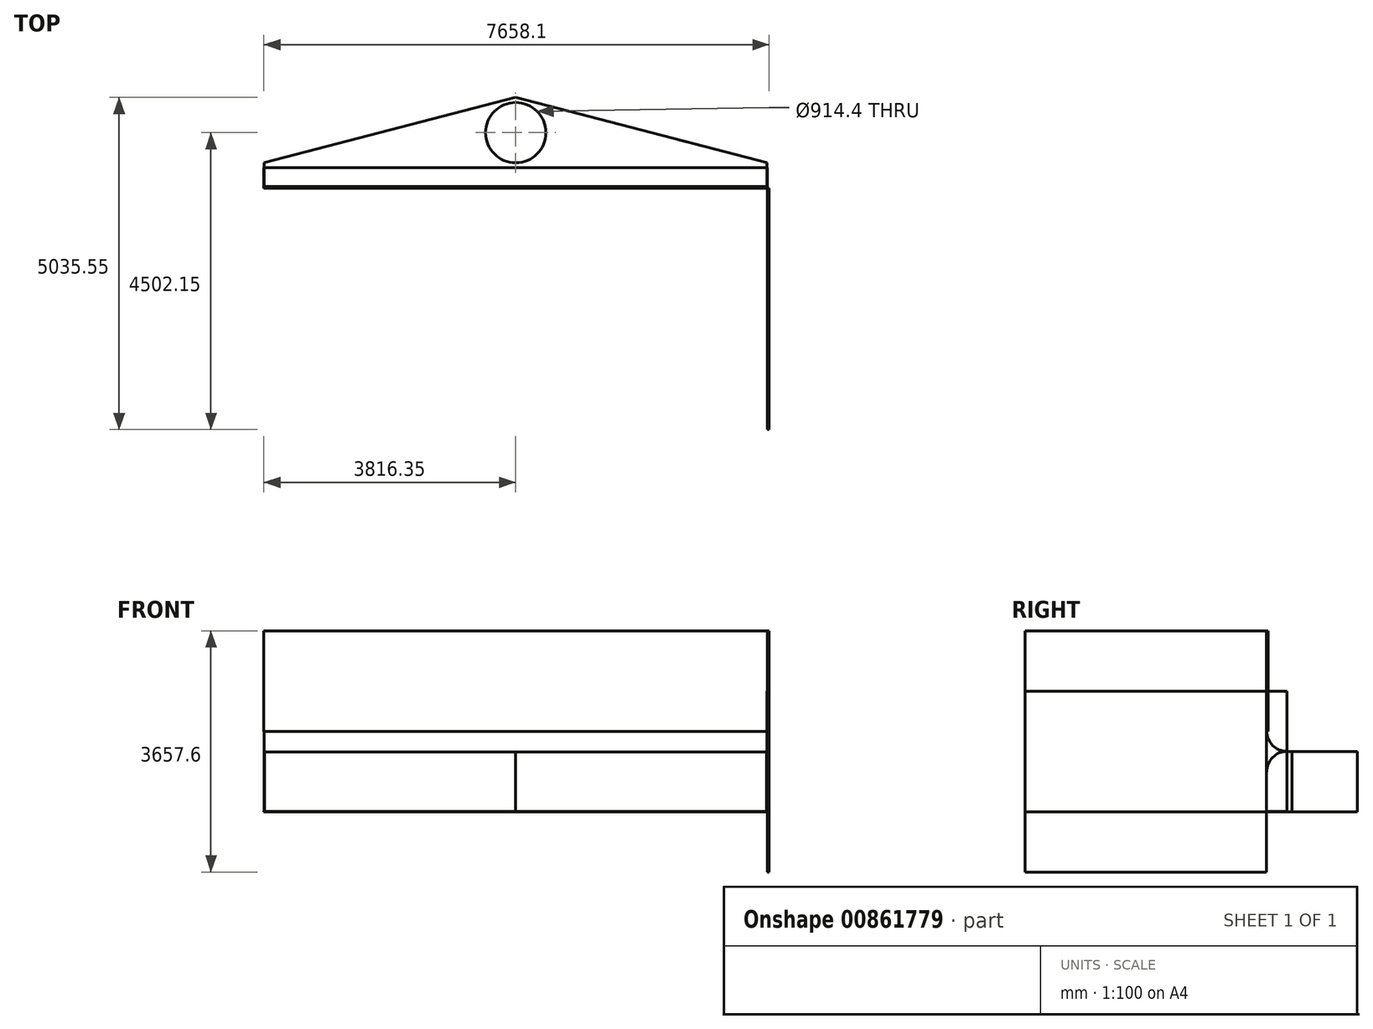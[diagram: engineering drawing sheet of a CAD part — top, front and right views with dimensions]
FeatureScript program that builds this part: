
annotation { "Feature Type Name" : "Feature", "Feature Type Description" : "" }
export const myFeature = defineFeature(function(context is Context, id is Id, definition is map)
    precondition{}
    {
        {
            var Q0;
            Q0=qCreatedBy(makeId("Front.planeOp"),FACE);
            var sketch = newSketch(context, id + "F0", { "sketchPlane" : qUnion([Q0])});
            skLineSegment(sketch, "E0", {"start": v(0, 0) * mm, "end": v(7620, 0) * mm});
            skLineSegment(sketch, "E1", {"start": v(7620, 0) * mm, "end": v(7620, 914.4) * mm});
            skLineSegment(sketch, "E2", {"start": v(7620, 914.4) * mm, "end": v(0, 914.4) * mm});
            skLineSegment(sketch, "E3", {"start": v(0, 914.4) * mm, "end": v(0, 0) * mm});
            skSolve(sketch);
        }
        {
            var Q0;
            Q0=makeQuery(id+"F0.imprint","IMPRINT",FACE,{"disambiguationData":[TD([[makeQuery(id+"F0.imprint","IMPRINT",EDGE,{"derivedFrom":sQuery(id+"F0.wireOp",EDGE,"E0")}),1.0]])]});
            extrude(context, id + "F1", {"entities" : qUnion([Q0]), "depth" : 1066.8 * mm, "offsetDistance" : 25.4 * mm});
        }
        {
            var Q0;
            Q0=makeQuery(id+"F1.opExtrude","SWEPT_FACE",FACE,{"disambiguationData":[OSD([sQuery(id+"F0.wireOp",EDGE,"E2")])]});
            var sketch = newSketch(context, id + "F2", { "sketchPlane" : qUnion([Q0])});
            skLineSegment(sketch, "E4", {"start": v(3810, 0) * mm, "end": v(3810, -533.4) * mm, "construction": true});
            skCircle(sketch, "E5", {"center": v(3810, -533.4) * mm, "radius": 457.2 * mm});
            skLineSegment(sketch, "E6.0", {"start": v(7620, -990.6) * mm, "end": v(0, -990.6) * mm, "construction": true});
            skLineSegment(sketch, "E7", {"start": v(3810, 0) * mm, "end": v(7620, -990.6) * mm});
            skLineSegment(sketch, "E8", {"start": v(3810, 0) * mm, "end": v(0, -990.6) * mm});
            skSolve(sketch);
        }
        {
            var Q0;
            {var subQ0=sQuery(id+"F2.wireOp",EDGE,"E7");Q0=makeQuery(id+"F2.imprint","IMPRINT",FACE,{"disambiguationData":[TD([[makeQuery(id+"F2.imprint","IMPRINT",EDGE,{"derivedFrom":subQ0}),1.0]])]});}
            var Q1;
            {var subQ0=sQuery(id+"F2.wireOp",EDGE,"E8");Q1=makeQuery(id+"F2.imprint","IMPRINT",FACE,{"disambiguationData":[TD([[makeQuery(id+"F2.imprint","IMPRINT",EDGE,{"derivedFrom":subQ0}),-1.0]])]});}
            var Q2;
            Q2=sQuery(id+"F2.wireOp",EDGE,"E7");
            extrude(context, id + "F3", {"entities" : qUnion([Q0, Q1]), "operationType" : NewBodyOperationType.REMOVE, "surfaceEntities" : qUnion([Q2]), "endBound" : BoundingType.THROUGH_ALL, "oppositeDirection" : true, "depth" : 25.4 * mm, "offsetDistance" : 25.4 * mm});
        }
        {
            var Q0;
            Q0=makeQuery(id+"F1.opExtrude","CAP_FACE",FACE,{"disambiguationData":[OSD([sQuery(id+"F0.wireOp",EDGE,"E0"),sQuery(id+"F0.wireOp",EDGE,"E1"),sQuery(id+"F0.wireOp",EDGE,"E2"),sQuery(id+"F0.wireOp",EDGE,"E3")])],"isStart":false});
            shell(context, id + "F4", {"entities" : qUnion([Q0]), "thickness" : 6.35 * mm});
        }
        {
            var Q0;
            Q0=makeQuery(id+"F2.imprint","IMPRINT",FACE,{"disambiguationData":[TD([[makeQuery(id+"F2.imprint","IMPRINT",EDGE,{"derivedFrom":sQuery(id+"F2.wireOp",EDGE,"E5")}),1.0]])]});
            extrude(context, id + "F5", {"entities" : qUnion([Q0]), "operationType" : NewBodyOperationType.REMOVE, "endBound" : BoundingType.UP_TO_NEXT, "oppositeDirection" : true, "depth" : 25.4 * mm, "offsetDistance" : 25.4 * mm});
        }
        {
            var Q0;
            Q0=makeQuery(id+"F1.opExtrude","SWEPT_FACE",FACE,{"disambiguationData":[OSD([sQuery(id+"F0.wireOp",EDGE,"E1")])]});
            var sketch = newSketch(context, id + "F6", { "sketchPlane" : qUnion([Q0])});
            skLineSegment(sketch, "E9", {"start": v(-1066.8, 914.4) * mm, "end": v(-1066.8, 1219.2) * mm, "construction": true});
            skArc(sketch, "E10", {"start": v(-1371.6, 1219.2) * mm, "mid": v(-1282.33, 1003.67) * mm, "end": v(-1066.8, 914.4) * mm});
            skLineSegment(sketch, "E11", {"start": v(-1066.8, 1219.2) * mm, "end": v(-1371.6, 1219.2) * mm, "construction": true});
            skArc(sketch, "E12.0", {"start": v(-1377.95, 1219.2) * mm, "mid": v(-1286.82, 999.18) * mm, "end": v(-1066.8, 908.05) * mm});
            skLineSegment(sketch, "E13", {"start": v(-1066.8, 908.05) * mm, "end": v(-1066.8, 914.4) * mm});
            skLineSegment(sketch, "E14", {"start": v(-1371.6, 1219.2) * mm, "end": v(-1377.95, 1219.2) * mm});
            skSolve(sketch);
        }
        {
            var Q0;
            Q0 = qSketchRegion(id + "F6", true);
            var Q1;
            Q1=makeQuery(id+"F1.opExtrude","CAP_VERTEX",VERTEX,{"disambiguationData":[OSD([sQuery(id+"F0.wireOp",EDGE,"E2"),sQuery(id+"F0.wireOp",EDGE,"E3")])],"isStart":false});
            extrude(context, id + "F7", {"entities" : qUnion([Q0]), "endBound" : BoundingType.UP_TO_VERTEX, "oppositeDirection" : true, "depth" : 25.4 * mm, "endBoundEntityVertex" : qUnion([Q1]), "offsetDistance" : 25.4 * mm});
        }
        {
            var Q0;
            Q0=makeQuery(id+"F7.opExtrude","CAP_FACE",FACE,{"disambiguationData":[OSD([sQuery(id+"F6.wireOp",EDGE,"E10"),sQuery(id+"F6.wireOp",EDGE,"E12.0"),sQuery(id+"F6.wireOp",EDGE,"E13"),sQuery(id+"F6.wireOp",EDGE,"E14")])],"isStart":true});
            var sketch = newSketch(context, id + "F8", { "sketchPlane" : qUnion([Q0])});
            skLineSegment(sketch, "E15", {"start": v(-1377.95, 1219.2) * mm, "end": v(-1377.95, 0) * mm});
            skLineSegment(sketch, "E16.1", {"start": v(-1066.8, 0) * mm, "end": v(-1066.8, 914.4) * mm});
            skLineSegment(sketch, "E17.1", {"start": v(-1371.6, 1219.2) * mm, "end": v(-1377.95, 1219.2) * mm});
            skArc(sketch, "E17.2", {"start": v(-1371.6, 1219.2) * mm, "mid": v(-1282.33, 1003.67) * mm, "end": v(-1066.8, 914.4) * mm});
            skLineSegment(sketch, "E18", {"start": v(-1066.8, 0) * mm, "end": v(-1377.95, 0) * mm});
            skSolve(sketch);
        }
        {
            var Q0;
            Q0=makeQuery(id+"F8.imprint","IMPRINT",FACE,{"disambiguationData":[TD([[makeQuery(id+"F8.imprint","IMPRINT",EDGE,{"derivedFrom":sQuery(id+"F8.wireOp",EDGE,"E17.1")}),1.0]])]});
            var Q1;
            Q1=makeQuery(id+"F8.imprint","IMPRINT",FACE,{"disambiguationData":[TD([[makeQuery(id+"F8.imprint","IMPRINT",EDGE,{"derivedFrom":sQuery(id+"F8.wireOp",EDGE,"E15")}),1.0]])]});
            extrude(context, id + "F9", {"entities" : qUnion([Q0, Q1]), "depth" : 6.35 * mm, "offsetDistance" : 25.4 * mm});
        }
        {
            var Q0;
            {var subQ0=sQuery(id+"F2.wireOp",EDGE,"E8");var subQ1=sQuery(id+"F2.wireOp",EDGE,"E7");var subQ2=sQuery(id+"F0.wireOp",EDGE,"E2");Q0=makeQuery(id+"F3.boolean.opBoolean","TWEAK_EDGE",EDGE,{"derivedFrom":[makeQuery(id+"F3.opExtrude","SWEPT_EDGE",EDGE,{"disambiguationData":[OSD([subQ2,subQ1,subQ0]),OD(0.0)]}),makeQuery(id+"F3.opExtrude","SWEPT_EDGE",EDGE,{"disambiguationData":[OSD([subQ2,subQ1,subQ0]),OD(1.0)]})]});}
            var Q1;
            Q1=sQuery(id+"F2.wireOp",EDGE,"E4");
            cPlane(context, id + "F10", {"entities" : qUnion([Q0, Q1]), "cplaneType" : CPlaneType.LINE_ANGLE, "offset" : 25.4 * mm, "angle" : 0 * degree, "width" : 152.4 * mm, "height" : 152.4 * mm});
        }
        {
            var Q0;
            Q0=makeQuery(id+"F9.opExtrude","SWEPT_BODY",BODY,{"disambiguationData":[OSD([sQuery(id+"F8.wireOp",EDGE,"E15"),sQuery(id+"F8.wireOp",EDGE,"E16.1"),sQuery(id+"F8.wireOp",EDGE,"E17.1"),sQuery(id+"F8.wireOp",EDGE,"E17.2"),sQuery(id+"F8.wireOp",EDGE,"E17.4"),sQuery(id+"F8.wireOp",EDGE,"E17.5")])]});
            var Q1;
            Q1=qCreatedBy(id+"F10.planeOp",FACE);
            mirror(context, id + "F11", {"entities" : qUnion([Q0]), "mirrorPlane" : qUnion([Q1])});
        }
        {
            var Q0;
            Q0=makeQuery(id+"F9.opExtrude","CAP_FACE",FACE,{"disambiguationData":[OSD([sQuery(id+"F8.wireOp",EDGE,"E15"),sQuery(id+"F8.wireOp",EDGE,"E16.1"),sQuery(id+"F8.wireOp",EDGE,"E17.1"),sQuery(id+"F8.wireOp",EDGE,"E17.2"),sQuery(id+"F8.wireOp",EDGE,"E18")])],"isStart":false});
            var sketch = newSketch(context, id + "F12", { "sketchPlane" : qUnion([Q0])});
            skSolve(sketch);
        }
        {
            var Q0;
            Q0=makeQuery(id+"F1.opExtrude","SWEPT_FACE",FACE,{"disambiguationData":[OSD([sQuery(id+"F0.wireOp",EDGE,"E0")])]});
            var sketch = newSketch(context, id + "F13", { "sketchPlane" : qUnion([Q0])});
            skLineSegment(sketch, "E19.bottom", {"start": v(-6.35, 1066.8) * mm, "end": v(7626.35, 1066.8) * mm});
            skLineSegment(sketch, "E19.top", {"start": v(-6.35, 1377.95) * mm, "end": v(7626.35, 1377.95) * mm});
            skLineSegment(sketch, "E19.left", {"start": v(-6.35, 1066.8) * mm, "end": v(-6.35, 1377.95) * mm});
            skLineSegment(sketch, "E19.right", {"start": v(7626.35, 1066.8) * mm, "end": v(7626.35, 1377.95) * mm});
            skSolve(sketch);
        }
        {
            var Q0;
            Q0=makeQuery(id+"F13.imprint","IMPRINT",FACE,{"disambiguationData":[TD([[makeQuery(id+"F13.imprint","IMPRINT",EDGE,{"derivedFrom":sQuery(id+"F13.wireOp",EDGE,"E19.top")}),-1.0]])]});
            extrude(context, id + "F14", {"entities" : qUnion([Q0]), "oppositeDirection" : true, "depth" : 6.35 * mm, "offsetDistance" : 25.4 * mm});
        }
        {
            var Q0;
            Q0=makeQuery(id+"F12.imprint","IMPRINT",FACE,{"disambiguationData":[TD([[makeQuery(id+"F12.imprint","IMPRINT",EDGE,{"derivedFrom":makeQuery(id+"F9.opExtrude","CAP_EDGE",EDGE,{"disambiguationData":[OSD([sQuery(id+"F8.wireOp",EDGE,"E15")])],"isStart":false})}),1.0]])]});
            var sketch = newSketch(context, id + "F15", { "sketchPlane" : qUnion([Q0])});
            skLineSegment(sketch, "E20.bottom", {"start": v(-1377.95, 2743.2) * mm, "end": v(-5035.55, 2743.2) * mm});
            skLineSegment(sketch, "E20.top", {"start": v(-1377.95, 0) * mm, "end": v(-5035.55, 0) * mm});
            skLineSegment(sketch, "E20.left", {"start": v(-1377.95, 2743.2) * mm, "end": v(-1377.95, 0) * mm});
            skLineSegment(sketch, "E20.right", {"start": v(-5035.55, 2743.2) * mm, "end": v(-5035.55, 0) * mm});
            skSolve(sketch);
        }
        {
            var Q0;
            {var subQ3=sQuery(id+"F15.wireOp",EDGE,"E20.top");Q0=makeQuery(id+"F15.imprint","IMPRINT",FACE,{"disambiguationData":[TD([[makeQuery(id+"F15.imprint","IMPRINT",EDGE,{"derivedFrom":subQ3}),-1.0]])]});}
            extrude(context, id + "F16", {"entities" : qUnion([Q0]), "depth" : 25.4 * mm, "offsetDistance" : 25.4 * mm});
        }
        {
            var Q0;
            Q0=makeQuery(id+"F16.opExtrude","SWEPT_BODY",BODY,{"disambiguationData":[OSD([sQuery(id+"F12.wireOp",EDGE,"kAEaOyA6-nG5r-lN2p-HJhC-7QTWJcD4QFZO.bottom"),sQuery(id+"F12.wireOp",EDGE,"kAEaOyA6-nG5r-lN2p-HJhC-7QTWJcD4QFZO.right"),sQuery(id+"F15.wireOp",EDGE,"E20.bottom"),sQuery(id+"F15.wireOp",EDGE,"E20.top"),sQuery(id+"F15.wireOp",EDGE,"E20.left"),sQuery(id+"F15.wireOp",EDGE,"E20.right")])]});
            var Q1;
            Q1=qCreatedBy(id+"F10.planeOp",FACE);
            mirror(context, id + "F17", {"entities" : qUnion([Q0]), "mirrorPlane" : qUnion([Q1])});
        }
        {
            var Q0;
            Q0=makeQuery(id+"F16.opExtrude","SWEPT_FACE",FACE,{"disambiguationData":[OSD([sQuery(id+"F15.wireOp",EDGE,"E20.left")])]});
            var sketch = newSketch(context, id + "F18", { "sketchPlane" : qUnion([Q0])});
            skLineSegment(sketch, "E21.bottom", {"start": v(-7626.35, 2743.2) * mm, "end": v(6.35, 2743.2) * mm});
            skLineSegment(sketch, "E21.top", {"start": v(-7626.35, 1219.2) * mm, "end": v(6.35, 1219.2) * mm});
            skLineSegment(sketch, "E21.left", {"start": v(-7626.35, 2743.2) * mm, "end": v(-7626.35, 1219.2) * mm});
            skLineSegment(sketch, "E21.right", {"start": v(6.35, 2743.2) * mm, "end": v(6.35, 1219.2) * mm});
            skSolve(sketch);
        }
        {
            var Q0;
            Q0 = qSketchRegion(id + "F18", true);
            extrude(context, id + "F19", {"entities" : qUnion([Q0]), "depth" : 25.4 * mm, "offsetDistance" : 25.4 * mm});
        }
    });
